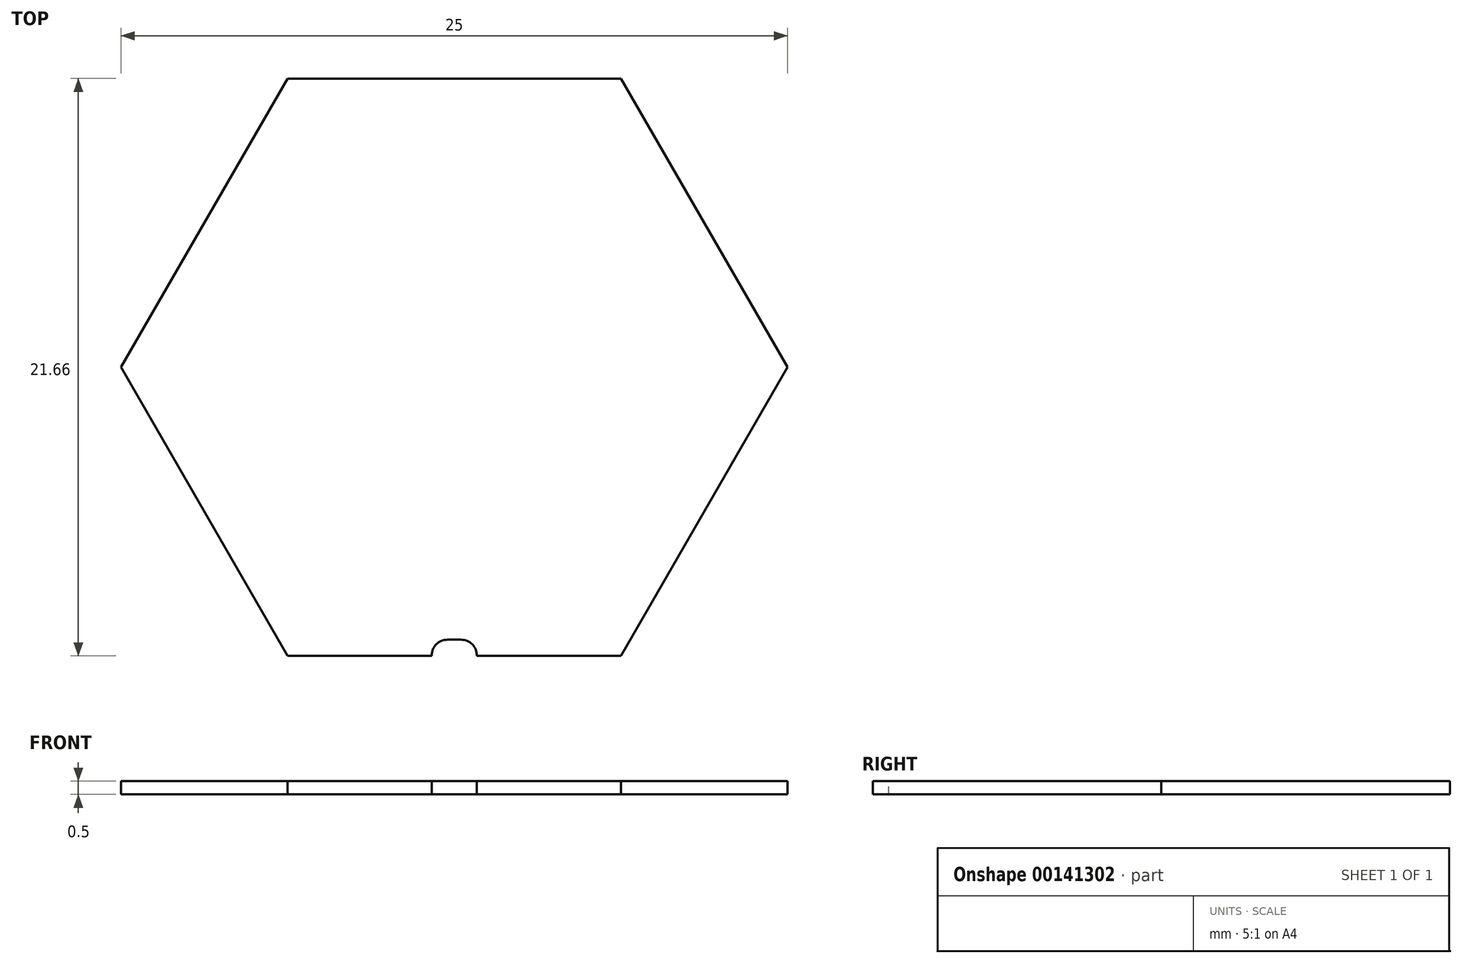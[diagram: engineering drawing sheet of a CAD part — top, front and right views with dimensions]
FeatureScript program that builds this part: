
annotation { "Feature Type Name" : "Feature", "Feature Type Description" : "" }
export const myFeature = defineFeature(function(context is Context, id is Id, definition is map)
    precondition{}
    {
        {
            var Q0;
            Q0=qCreatedBy(makeId("Top.planeOp"),FACE);
            var sketch = newSketch(context, id + "F0", { "sketchPlane" : qUnion([Q0])});
            skCircle(sketch, "E0.cCircle", {"center": v(0, 0) * mm, "radius": 12.5 * mm, "construction": true});
            skLineSegment(sketch, "E0.0", {"start": v(12.5, 0) * mm, "end": v(6.25, -10.83) * mm});
            skLineSegment(sketch, "E0.1", {"start": v(6.25, -10.83) * mm, "end": v(-6.25, -10.83) * mm});
            skLineSegment(sketch, "E0.2", {"start": v(-6.25, -10.83) * mm, "end": v(-12.5, 0) * mm});
            skLineSegment(sketch, "E0.3", {"start": v(-12.5, 0) * mm, "end": v(-6.25, 10.83) * mm});
            skLineSegment(sketch, "E0.4", {"start": v(-6.25, 10.83) * mm, "end": v(6.25, 10.83) * mm});
            skLineSegment(sketch, "E0.5", {"start": v(6.25, 10.83) * mm, "end": v(12.5, 0) * mm});
            skSolve(sketch);
        }
        {
            var Q0;
            Q0 = qSketchRegion(id + "F0", true);
            extrude(context, id + "F1", {"entities" : qUnion([Q0]), "depth" : 0.5 * mm});
        }
        {
            var Q0;
            Q0=makeQuery(id+"F1.opExtrude","CAP_FACE",FACE,{"disambiguationData":[OSD([sQuery(id+"F0.wireOp",EDGE,"E0.0"),sQuery(id+"F0.wireOp",EDGE,"E0.1"),sQuery(id+"F0.wireOp",EDGE,"E0.2"),sQuery(id+"F0.wireOp",EDGE,"E0.3"),sQuery(id+"F0.wireOp",EDGE,"E0.4"),sQuery(id+"F0.wireOp",EDGE,"E0.5")])],"isStart":false});
            var sketch = newSketch(context, id + "F2", { "sketchPlane" : qUnion([Q0])});
            skLineSegment(sketch, "E1.0", {"start": v(6.25, -10.83) * mm, "end": v(-6.25, -10.83) * mm, "construction": true});
            skLineSegment(sketch, "E2", {"start": v(0.25, -10.23) * mm, "end": v(-0.25, -10.23) * mm});
            skArc(sketch, "E3", {"start": v(-0.25, -10.23) * mm, "mid": v(-0.67, -10.4) * mm, "end": v(-0.85, -10.83) * mm});
            skArc(sketch, "E4", {"start": v(0.85, -10.83) * mm, "mid": v(0.67, -10.4) * mm, "end": v(0.25, -10.23) * mm});
            skLineSegment(sketch, "E5", {"start": v(-0.85, -10.83) * mm, "end": v(0.85, -10.83) * mm});
            skSolve(sketch);
        }
        {
            var Q0;
            Q0=makeQuery(id+"F2.imprint","IMPRINT",FACE,{"disambiguationData":[TD([[makeQuery(id+"F2.imprint","IMPRINT",EDGE,{"derivedFrom":sQuery(id+"F2.wireOp",EDGE,"E2")}),1.0]])]});
            extrude(context, id + "F3", {"entities" : qUnion([Q0]), "operationType" : NewBodyOperationType.REMOVE, "endBound" : BoundingType.THROUGH_ALL, "oppositeDirection" : true, "depth" : 25 * mm});
        }
    });
